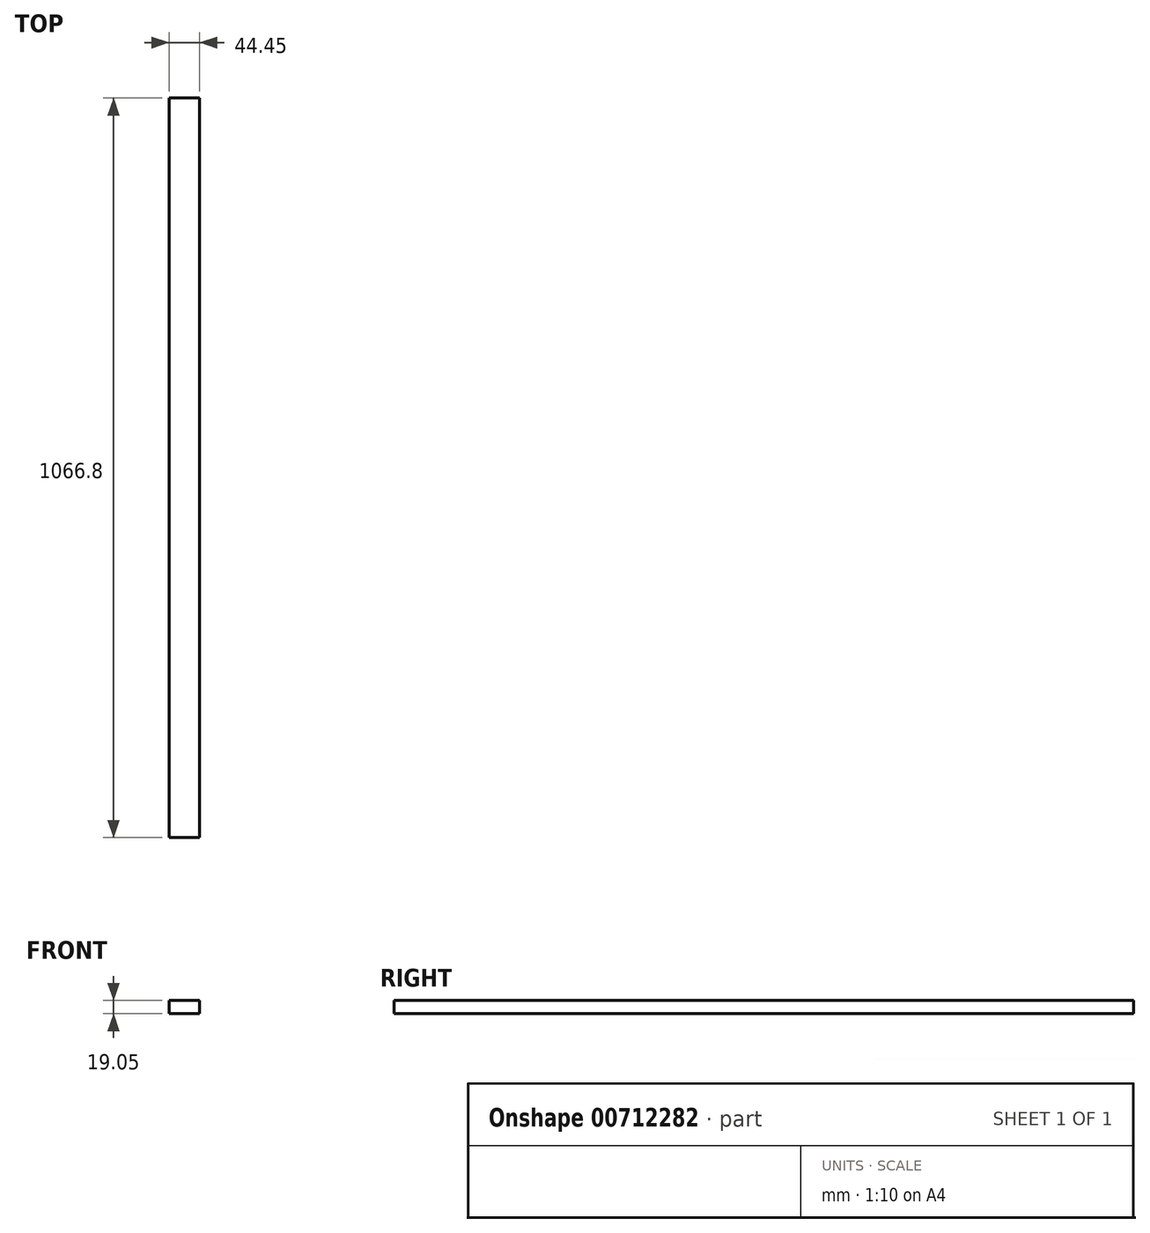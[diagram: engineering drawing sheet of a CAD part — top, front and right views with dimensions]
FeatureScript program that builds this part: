
annotation { "Feature Type Name" : "Feature", "Feature Type Description" : "" }
export const myFeature = defineFeature(function(context is Context, id is Id, definition is map)
    precondition{}
    {
        {
            var Q0;
            Q0=qCreatedBy(makeId("Front.planeOp"),FACE);
            var sketch = newSketch(context, id + "F0", { "sketchPlane" : qUnion([Q0])});
            skLineSegment(sketch, "E0.bottom", {"start": v(-52.17, 37.16) * mm, "end": v(-7.72, 37.16) * mm});
            skLineSegment(sketch, "E0.top", {"start": v(-52.17, 18.1) * mm, "end": v(-7.72, 18.1) * mm});
            skLineSegment(sketch, "E0.left", {"start": v(-52.17, 37.16) * mm, "end": v(-52.17, 18.1) * mm});
            skLineSegment(sketch, "E0.right", {"start": v(-7.72, 37.16) * mm, "end": v(-7.72, 18.1) * mm});
            skSolve(sketch);
        }
        {
            var Q0;
            Q0 = qSketchRegion(id + "F0", true);
            extrude(context, id + "F1", {"entities" : qUnion([Q0]), "depth" : 1066.8 * mm, "offsetDistance" : 25.4 * mm});
        }
    });
